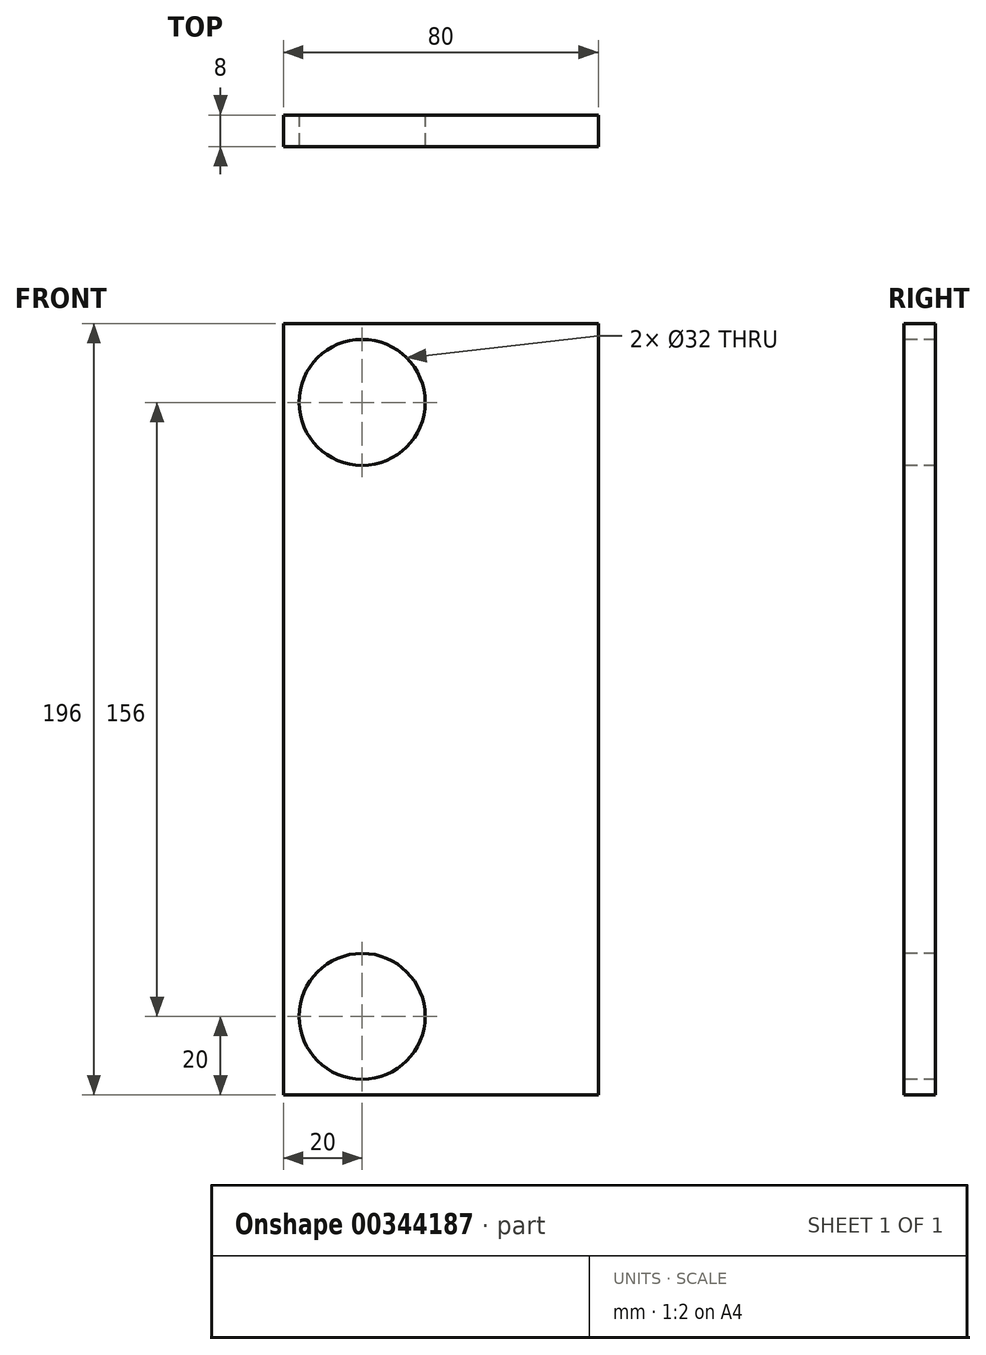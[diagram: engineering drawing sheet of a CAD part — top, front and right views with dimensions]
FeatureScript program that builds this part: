
annotation { "Feature Type Name" : "Feature", "Feature Type Description" : "" }
export const myFeature = defineFeature(function(context is Context, id is Id, definition is map)
    precondition{}
    {
        {
            var Q0;
            Q0=qCreatedBy(makeId("Front.planeOp"),FACE);
            var sketch = newSketch(context, id + "F0", { "sketchPlane" : qUnion([Q0])});
            skLineSegment(sketch, "E0.bottom", {"start": v(40, -98) * mm, "end": v(-40, -98) * mm});
            skLineSegment(sketch, "E0.top", {"start": v(40, 98) * mm, "end": v(-40, 98) * mm});
            skLineSegment(sketch, "E0.left", {"start": v(40, -98) * mm, "end": v(40, 98) * mm});
            skLineSegment(sketch, "E0.right", {"start": v(-40, -98) * mm, "end": v(-40, 98) * mm});
            skPoint(sketch, "E0.middle", {"position": v(0, 0) * mm});
            skSolve(sketch);
        }
        {
            var Q0;
            Q0 = qSketchRegion(id + "F0", true);
            extrude(context, id + "F1", {"entities" : qUnion([Q0]), "depth" : 8 * mm});
        }
        {
            var Q0;
            Q0=makeQuery(id+"F1.opExtrude","CAP_FACE",FACE,{"disambiguationData":[OSD([sQuery(id+"F0.wireOp",EDGE,"E0.bottom"),sQuery(id+"F0.wireOp",EDGE,"E0.top"),sQuery(id+"F0.wireOp",EDGE,"E0.left"),sQuery(id+"F0.wireOp",EDGE,"E0.right")])],"isStart":false});
            var sketch = newSketch(context, id + "F2", { "sketchPlane" : qUnion([Q0])});
            skLineSegment(sketch, "E1", {"start": v(-20, 113.99) * mm, "end": v(-20, -143.41) * mm, "construction": true});
            skCircle(sketch, "E2", {"center": v(-20, 78) * mm, "radius": 16 * mm});
            skCircle(sketch, "E3", {"center": v(-20, -78) * mm, "radius": 16 * mm});
            skSolve(sketch);
        }
        {
            var Q0;
            Q0 = qSketchRegion(id + "F2", true);
            extrude(context, id + "F3", {"entities" : qUnion([Q0]), "operationType" : NewBodyOperationType.REMOVE, "oppositeDirection" : true, "depth" : 25 * mm});
        }
    });
